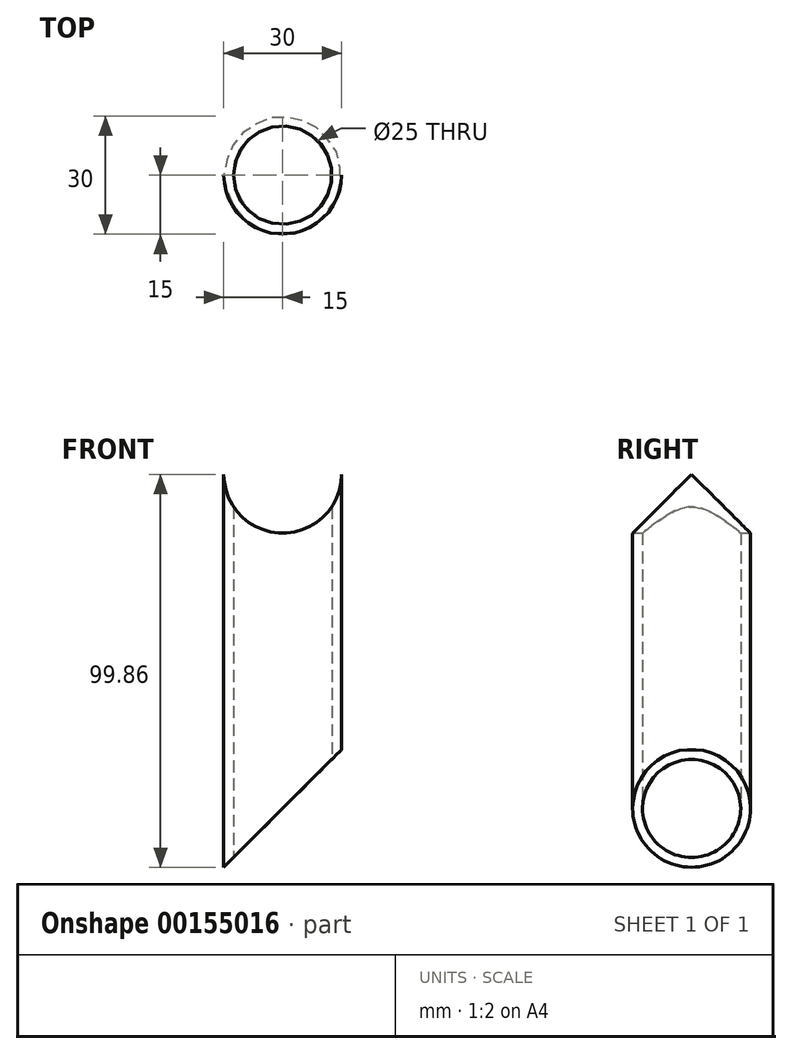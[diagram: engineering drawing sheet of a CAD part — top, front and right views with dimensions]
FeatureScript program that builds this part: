
annotation { "Feature Type Name" : "Feature", "Feature Type Description" : "" }
export const myFeature = defineFeature(function(context is Context, id is Id, definition is map)
    precondition{}
    {
        {
            var Q0;
            Q0=qCreatedBy(makeId("Top.planeOp"),FACE);
            var sketch = newSketch(context, id + "F0", { "sketchPlane" : qUnion([Q0])});
            skCircle(sketch, "E0", {"center": v(0, 0) * mm, "radius": 15 * mm});
            skCircle(sketch, "E1", {"center": v(0, 0) * mm, "radius": 12.5 * mm});
            skSolve(sketch);
        }
        {
            var Q0;
            Q0 = qSketchRegion(id + "F0", true);
            extrude(context, id + "F1", {"entities" : qUnion([Q0]), "endBound" : BoundingType.SYMMETRIC, "depth" : 99.85 * mm});
        }
        {
            var Q0;
            Q0=qCreatedBy(makeId("Front.planeOp"),FACE);
            var sketch = newSketch(context, id + "F2", { "sketchPlane" : qUnion([Q0])});
            skCircle(sketch, "E2", {"center": v(0, 49.93) * mm, "radius": 15 * mm});
            skSolve(sketch);
        }
        {
            var Q0;
            Q0=makeQuery(id+"F2.imprint","IMPRINT",FACE,{"disambiguationData":[TD([[makeQuery(id+"F2.imprint","IMPRINT",EDGE,{"derivedFrom":sQuery(id+"F2.wireOp",EDGE,"E2")}),1.0]])]});
            extrude(context, id + "F3", {"entities" : qUnion([Q0]), "operationType" : NewBodyOperationType.REMOVE, "endBound" : BoundingType.SYMMETRIC, "oppositeDirection" : true, "depth" : 50 * mm});
        }
        {
            var Q0;
            Q0=qCreatedBy(makeId("Front.planeOp"),FACE);
            var sketch = newSketch(context, id + "F4", { "sketchPlane" : qUnion([Q0])});
            skLineSegment(sketch, "E3.0", {"start": v(-15, -49.93) * mm, "end": v(15, -49.93) * mm});
            skLineSegment(sketch, "E4", {"start": v(-15, -49.93) * mm, "end": v(15, -19.93) * mm});
            skLineSegment(sketch, "E5", {"start": v(15, -49.93) * mm, "end": v(15, -19.93) * mm});
            skSolve(sketch);
        }
        {
            var Q0;
            Q0=makeQuery(id+"F4.imprint","IMPRINT",FACE,{"disambiguationData":[TD([[makeQuery(id+"F4.imprint","IMPRINT",EDGE,{"derivedFrom":sQuery(id+"F4.wireOp",EDGE,"E3.0")}),1.0]])]});
            var Q1;
            Q1=sQuery(id+"F4.wireOp",EDGE,"E4");
            var Q2;
            Q2=sQuery(id+"F4.wireOp",EDGE,"E5");
            var Q3;
            Q3=sQuery(id+"F4.wireOp",EDGE,"E3.0");
            extrude(context, id + "F5", {"entities" : qUnion([Q0]), "operationType" : NewBodyOperationType.REMOVE, "surfaceEntities" : qUnion([Q1, Q2, Q3]), "endBound" : BoundingType.SYMMETRIC, "depth" : 30 * mm});
        }
        {
            var Q0;
            Q0 = qSketchRegion(id + "F4", true);
            extrude(context, id + "F6", {"entities" : qUnion([Q0]), "operationType" : NewBodyOperationType.REMOVE, "endBound" : BoundingType.SYMMETRIC, "oppositeDirection" : true, "depth" : 50 * mm});
        }
    });
